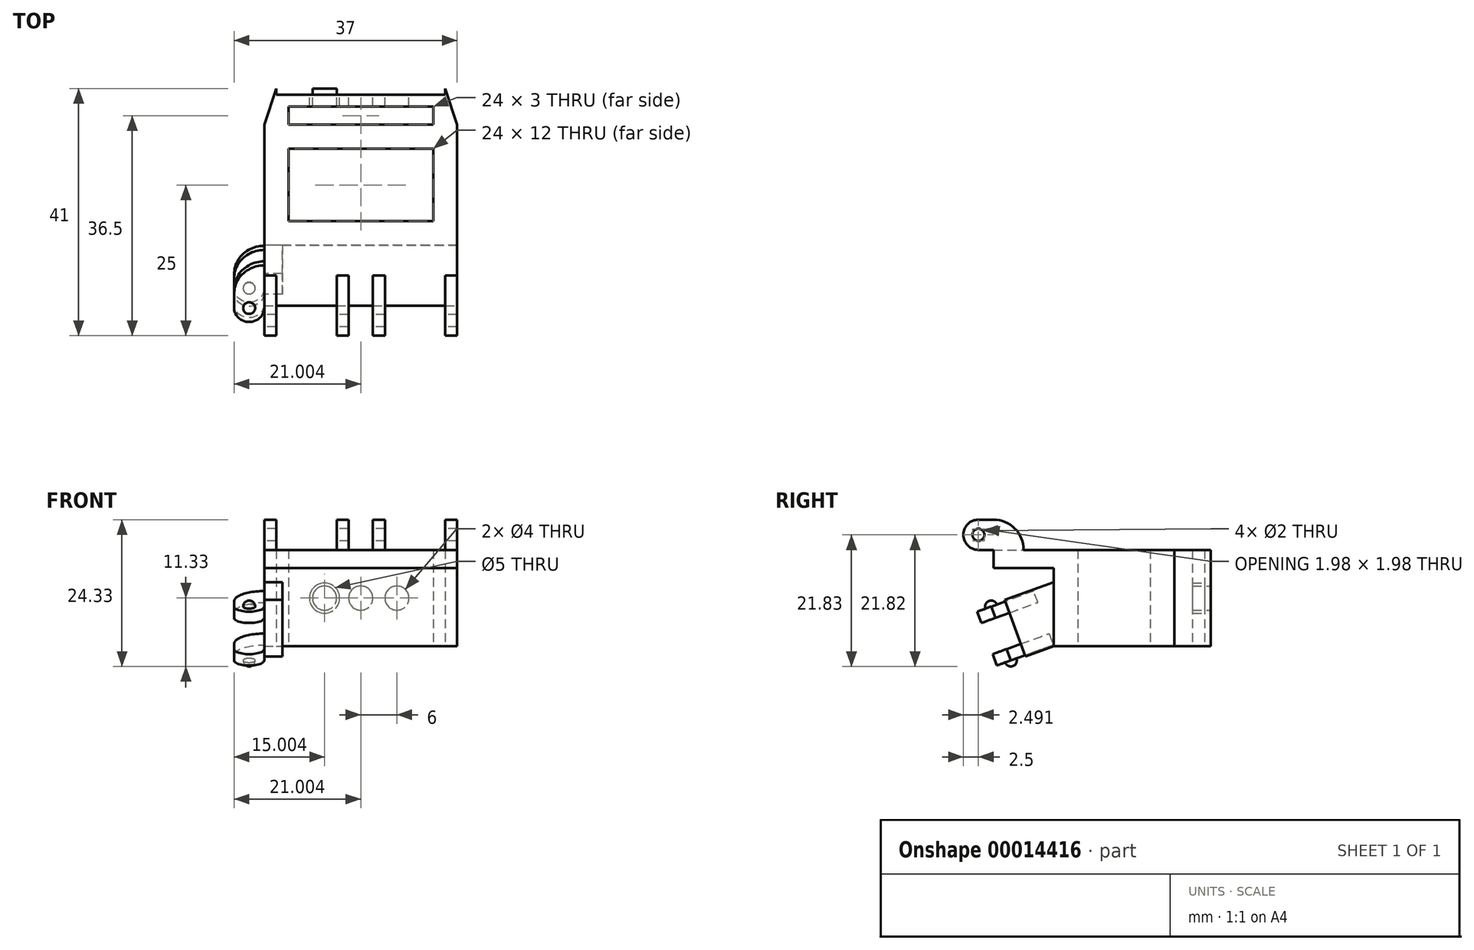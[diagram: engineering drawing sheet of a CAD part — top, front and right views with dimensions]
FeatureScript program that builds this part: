
annotation { "Feature Type Name" : "Feature", "Feature Type Description" : "" }
export const myFeature = defineFeature(function(context is Context, id is Id, definition is map)
    precondition{}
    {
        {
            var Q0;
            Q0=qCreatedBy(makeId("Top.planeOp"),FACE);
            var sketch = newSketch(context, id + "F0", { "sketchPlane" : qUnion([Q0])});
            skLineSegment(sketch, "E0.bottom", {"start": v(-11.62, 6.4) * mm, "end": v(12.38, 6.4) * mm});
            skLineSegment(sketch, "E0.top", {"start": v(-11.62, -5.6) * mm, "end": v(12.38, -5.6) * mm});
            skLineSegment(sketch, "E0.left", {"start": v(-11.62, 6.4) * mm, "end": v(-11.62, -5.6) * mm});
            skLineSegment(sketch, "E0.right", {"start": v(12.38, 6.4) * mm, "end": v(12.38, -5.6) * mm});
            skLineSegment(sketch, "E1.0", {"start": v(-15.62, 10.4) * mm, "end": v(16.38, 10.4) * mm});
            skLineSegment(sketch, "E1.1", {"start": v(-15.62, 10.4) * mm, "end": v(-15.62, -9.6) * mm});
            skLineSegment(sketch, "E1.2", {"start": v(-15.62, -9.6) * mm, "end": v(16.38, -9.6) * mm});
            skLineSegment(sketch, "E1.3", {"start": v(16.38, 10.4) * mm, "end": v(16.38, -9.6) * mm});
            skLineSegment(sketch, "E2", {"start": v(0.38, 10.4) * mm, "end": v(0.38, 16) * mm, "construction": true});
            skPoint(sketch, "E3", {"position": v(0.38, 13.4) * mm});
            skPoint(sketch, "E4", {"position": v(12.38, 10.4) * mm});
            skLineSegment(sketch, "E5", {"start": v(12.38, 10.4) * mm, "end": v(12.38, 13.4) * mm});
            skLineSegment(sketch, "E6", {"start": v(0.38, 13.4) * mm, "end": v(12.38, 13.4) * mm});
            skLineSegment(sketch, "E7.MirrorCS", {"start": v(0.38, 13.4) * mm, "end": v(-11.62, 13.4) * mm});
            skLineSegment(sketch, "E8.MirrorCS", {"start": v(-11.62, 10.4) * mm, "end": v(-11.62, 13.4) * mm});
            skPoint(sketch, "E9", {"position": v(0.38, 16.4) * mm});
            skLineSegment(sketch, "E10", {"start": v(0.38, 16.4) * mm, "end": v(14.38, 16.4) * mm});
            skLineSegment(sketch, "E11", {"start": v(16.38, 10.4) * mm, "end": v(14.38, 16.4) * mm});
            skLineSegment(sketch, "E12.MirrorCS", {"start": v(0.38, 16.4) * mm, "end": v(-13.62, 16.4) * mm});
            skLineSegment(sketch, "E13.MirrorCS", {"start": v(-15.62, 10.4) * mm, "end": v(-13.62, 16.4) * mm});
            skSolve(sketch);
        }
        {
            var Q0;
            Q0=makeQuery(id+"F0.imprint","IMPRINT",FACE,{"disambiguationData":[TD([[makeQuery(id+"F0.imprint","IMPRINT",EDGE,{"derivedFrom":sQuery(id+"F0.wireOp",EDGE,"E0.bottom")}),1.0]])]});
            var Q1;
            Q1=makeQuery(id+"F0.imprint","IMPRINT",FACE,{"disambiguationData":[TD([[makeQuery(id+"F0.imprint","IMPRINT",EDGE,{"derivedFrom":sQuery(id+"F0.wireOp",EDGE,"d9226599-e2ed-4d66-8e42-112def7345b0")}),1.0]])]});
            var Q2;
            {var subQ3=sQuery(id+"F0.wireOp",EDGE,"E5");Q2=makeQuery(id+"F0.imprint","IMPRINT",FACE,{"disambiguationData":[TD([[makeQuery(id+"F0.imprint","IMPRINT",EDGE,{"derivedFrom":subQ3}),-1.0]])]});}
            extrude(context, id + "F1", {"entities" : qUnion([Q0, Q1, Q2]), "depth" : 16 * mm});
        }
        {
            var Q0;
            Q0=makeQuery(id+"F1.opExtrude","SWEPT_FACE",FACE,{"disambiguationData":[OSD([sQuery(id+"F0.wireOp",EDGE,"E10"),sQuery(id+"F0.wireOp",EDGE,"E12.MirrorCS")])]});
            var sketch = newSketch(context, id + "F2", { "sketchPlane" : qUnion([Q0])});
            skLineSegment(sketch, "E14", {"start": v(-0.38, 16) * mm, "end": v(-0.38, 0) * mm, "construction": true});
            skLineSegment(sketch, "E15", {"start": v(-14.88, 8) * mm, "end": v(14.12, 8) * mm, "construction": true});
            skCircle(sketch, "E16", {"center": v(-0.38, 8) * mm, "radius": 2.5 * mm});
            skCircle(sketch, "E17", {"center": v(-0.38, 8) * mm, "radius": 2 * mm});
            skCircle(sketch, "E18", {"center": v(-6.38, 8) * mm, "radius": 2.5 * mm});
            skCircle(sketch, "E19", {"center": v(-6.38, 8) * mm, "radius": 2 * mm});
            skCircle(sketch, "E20.MirrorC", {"center": v(5.62, 8) * mm, "radius": 2.5 * mm});
            skCircle(sketch, "E21.MirrorC", {"center": v(5.62, 8) * mm, "radius": 2 * mm});
            skPoint(sketch, "E22", {"position": v(-14.38, 0) * mm});
            skPoint(sketch, "E23", {"position": v(13.62, 0) * mm});
            skLineSegment(sketch, "E24", {"start": v(-14.38, 16) * mm, "end": v(13.62, 0) * mm, "construction": true});
            skLineSegment(sketch, "E25", {"start": v(-14.38, 0) * mm, "end": v(13.62, 16) * mm, "construction": true});
            skSolve(sketch);
        }
        {
            var Q0;
            Q0=makeQuery(id+"F2.imprint","IMPRINT",FACE,{"disambiguationData":[TD([[makeQuery(id+"F2.imprint","IMPRINT",EDGE,{"derivedFrom":sQuery(id+"F2.wireOp",EDGE,"E19")}),1.0]])]});
            var Q1;
            Q1=makeQuery(id+"F2.imprint","IMPRINT",FACE,{"disambiguationData":[TD([[makeQuery(id+"F2.imprint","IMPRINT",EDGE,{"derivedFrom":sQuery(id+"F2.wireOp",EDGE,"E17")}),1.0]])]});
            var Q2;
            Q2=makeQuery(id+"F2.imprint","IMPRINT",FACE,{"disambiguationData":[TD([[makeQuery(id+"F2.imprint","IMPRINT",EDGE,{"derivedFrom":sQuery(id+"F2.wireOp",EDGE,"E21.MirrorC")}),-1.0]])]});
            extrude(context, id + "F3", {"entities" : qUnion([Q0, Q1, Q2]), "operationType" : NewBodyOperationType.REMOVE, "endBound" : BoundingType.UP_TO_NEXT, "oppositeDirection" : true, "depth" : 25 * mm});
        }
        {
            var Q0;
            Q0=makeQuery(id+"F2.imprint","IMPRINT",FACE,{"disambiguationData":[TD([[makeQuery(id+"F2.imprint","IMPRINT",EDGE,{"derivedFrom":sQuery(id+"F2.wireOp",EDGE,"E18")}),1.0]])]});
            var Q1;
            Q1=makeQuery(id+"F2.imprint","IMPRINT",FACE,{"disambiguationData":[TD([[makeQuery(id+"F2.imprint","IMPRINT",EDGE,{"derivedFrom":sQuery(id+"F2.wireOp",EDGE,"E20.MirrorC")}),-1.0]])]});
            var Q2;
            Q2=makeQuery(id+"F2.imprint","IMPRINT",FACE,{"disambiguationData":[TD([[makeQuery(id+"F2.imprint","IMPRINT",EDGE,{"derivedFrom":sQuery(id+"F2.wireOp",EDGE,"E16")}),1.0]])]});
            extrude(context, id + "F4", {"entities" : qUnion([Q0, Q1, Q2]), "operationType" : NewBodyOperationType.REMOVE, "oppositeDirection" : true, "depth" : 1 * mm});
        }
        {
            var Q0;
            Q0=makeQuery(id+"F1.opExtrude","SWEPT_FACE",FACE,{"disambiguationData":[OSD([sQuery(id+"F0.wireOp",EDGE,"E1.2")])]});
            var sketch = newSketch(context, id + "F5", { "sketchPlane" : qUnion([Q0])});
            skPoint(sketch, "E26", {"position": v(-15.62, 16) * mm});
            skPoint(sketch, "E27", {"position": v(-15.62, 13) * mm});
            skPoint(sketch, "E28", {"position": v(-12.62, 16) * mm});
            skLineSegment(sketch, "E29", {"start": v(-12.62, 16) * mm, "end": v(-12.62, 0) * mm, "construction": true});
            skLineSegment(sketch, "E30", {"start": v(-15.62, 13) * mm, "end": v(16.38, 13) * mm, "construction": true});
            skPoint(sketch, "E31", {"position": v(-12.62, 13) * mm});
            skLineSegment(sketch, "E32", {"start": v(16.38, 13) * mm, "end": v(-12.62, 13) * mm});
            skLineSegment(sketch, "E33", {"start": v(-12.62, 0) * mm, "end": v(-12.62, 13) * mm});
            skLineSegment(sketch, "E34", {"start": v(-15.62, 0) * mm, "end": v(-12.62, 0) * mm});
            skLineSegment(sketch, "E35", {"start": v(-15.62, 0) * mm, "end": v(-15.62, 16) * mm});
            skLineSegment(sketch, "E36", {"start": v(-15.62, 16) * mm, "end": v(16.38, 16) * mm});
            skLineSegment(sketch, "E37", {"start": v(16.38, 16) * mm, "end": v(16.38, 13) * mm});
            skSolve(sketch);
        }
        {
            var Q0;
            Q0=makeQuery(id+"F5.imprint","IMPRINT",FACE,{"disambiguationData":[TD([[makeQuery(id+"F5.imprint","IMPRINT",EDGE,{"derivedFrom":sQuery(id+"F5.wireOp",EDGE,"E32")}),-1.0]])]});
            extrude(context, id + "F6", {"entities" : qUnion([Q0]), "operationType" : NewBodyOperationType.ADD, "depth" : 10 * mm});
        }
        {
            var Q0;
            Q0=makeQuery(id+"F6.boolean.opBoolean","MERGE",FACE,{"derivedFrom":[makeQuery(id+"F1.opExtrude","CAP_FACE",FACE,{"disambiguationData":[OSD([sQuery(id+"F0.wireOp",EDGE,"E0.bottom"),sQuery(id+"F0.wireOp",EDGE,"E0.top"),sQuery(id+"F0.wireOp",EDGE,"E0.left"),sQuery(id+"F0.wireOp",EDGE,"E0.right"),sQuery(id+"F0.wireOp",EDGE,"E1.0"),sQuery(id+"F0.wireOp",EDGE,"E1.1"),sQuery(id+"F0.wireOp",EDGE,"E1.2"),sQuery(id+"F0.wireOp",EDGE,"E1.3"),sQuery(id+"F0.wireOp",EDGE,"E5"),sQuery(id+"F0.wireOp",EDGE,"E6"),sQuery(id+"F0.wireOp",EDGE,"E7.MirrorCS"),sQuery(id+"F0.wireOp",EDGE,"E8.MirrorCS"),sQuery(id+"F0.wireOp",EDGE,"E10"),sQuery(id+"F0.wireOp",EDGE,"E11"),sQuery(id+"F0.wireOp",EDGE,"E12.MirrorCS"),sQuery(id+"F0.wireOp",EDGE,"E13.MirrorCS")])],"isStart":false}),makeQuery(id+"F6.opExtrude","SWEPT_FACE",FACE,{"disambiguationData":[OSD([sQuery(id+"F5.wireOp",EDGE,"E36")])]})]});
            var sketch = newSketch(context, id + "F7", { "sketchPlane" : qUnion([Q0])});
            skPoint(sketch, "E38", {"position": v(-15.62, -19.6) * mm});
            skPoint(sketch, "E39", {"position": v(-13.62, -19.6) * mm});
            skPoint(sketch, "E40", {"position": v(0.38, -19.6) * mm});
            skLineSegment(sketch, "E41", {"start": v(-15.62, -19.6) * mm, "end": v(-15.62, -24.6) * mm, "construction": true});
            skLineSegment(sketch, "E42", {"start": v(-13.62, -19.6) * mm, "end": v(-13.62, -24.6) * mm, "construction": true});
            skLineSegment(sketch, "E43", {"start": v(-15.62, -19.6) * mm, "end": v(-15.62, -14.6) * mm, "construction": true});
            skLineSegment(sketch, "E44", {"start": v(-13.62, -19.6) * mm, "end": v(-13.62, -14.6) * mm, "construction": true});
            skLineSegment(sketch, "E45", {"start": v(-15.62, -14.6) * mm, "end": v(-13.62, -14.6) * mm});
            skLineSegment(sketch, "E46", {"start": v(-13.62, -24.6) * mm, "end": v(-13.62, -14.6) * mm});
            skLineSegment(sketch, "E47", {"start": v(-15.62, -24.6) * mm, "end": v(-15.62, -14.6) * mm});
            skLineSegment(sketch, "E48", {"start": v(-15.62, -24.6) * mm, "end": v(-13.62, -24.6) * mm});
            skLineSegment(sketch, "E49", {"start": v(0.38, -19.6) * mm, "end": v(0.38, -13.68) * mm, "construction": true});
            skLineSegment(sketch, "E50.MirrorCS", {"start": v(14.38, -24.6) * mm, "end": v(14.38, -14.6) * mm});
            skLineSegment(sketch, "E51.MirrorCS", {"start": v(16.38, -24.6) * mm, "end": v(16.38, -14.6) * mm});
            skLineSegment(sketch, "E52.MirrorCS", {"start": v(16.38, -14.6) * mm, "end": v(14.38, -14.6) * mm});
            skLineSegment(sketch, "E53.MirrorCS", {"start": v(16.38, -24.6) * mm, "end": v(14.38, -24.6) * mm});
            skPoint(sketch, "E54", {"position": v(-8.62, -19.6) * mm});
            skLineSegment(sketch, "E55", {"start": v(-8.62, -19.6) * mm, "end": v(-8.62, -14.6) * mm, "construction": true});
            skLineSegment(sketch, "E56.MirrorCS", {"start": v(-1.62, -24.6) * mm, "end": v(-1.62, -14.6) * mm});
            skLineSegment(sketch, "E57.MirrorCS", {"start": v(-3.62, -24.6) * mm, "end": v(-3.62, -14.6) * mm});
            skLineSegment(sketch, "E58.MirrorCS", {"start": v(-1.62, -24.6) * mm, "end": v(-3.62, -24.6) * mm});
            skLineSegment(sketch, "E59.MirrorCS", {"start": v(-1.62, -14.6) * mm, "end": v(-3.62, -14.6) * mm});
            skLineSegment(sketch, "E60.MirrorCS", {"start": v(2.38, -24.6) * mm, "end": v(2.38, -14.6) * mm});
            skLineSegment(sketch, "E61.MirrorCS", {"start": v(4.38, -24.6) * mm, "end": v(4.38, -14.6) * mm});
            skLineSegment(sketch, "E62.MirrorCS", {"start": v(2.38, -14.6) * mm, "end": v(4.38, -14.6) * mm});
            skLineSegment(sketch, "E63.MirrorCS", {"start": v(2.38, -24.6) * mm, "end": v(4.38, -24.6) * mm});
            skSolve(sketch);
        }
        {
            var Q0;
            {var subQ5=sQuery(id+"F7.wireOp",EDGE,"E45");Q0=makeQuery(id+"F7.imprint","IMPRINT",FACE,{"disambiguationData":[TD([[makeQuery(id+"F7.imprint","IMPRINT",EDGE,{"derivedFrom":subQ5}),-1.0]])]});}
            var Q1;
            {var subQ5=sQuery(id+"F7.wireOp",EDGE,"E48");Q1=makeQuery(id+"F7.imprint","IMPRINT",FACE,{"disambiguationData":[TD([[makeQuery(id+"F7.imprint","IMPRINT",EDGE,{"derivedFrom":subQ5}),1.0]])]});}
            var Q2;
            {var subQ5=sQuery(id+"F7.wireOp",EDGE,"E53.MirrorCS");Q2=makeQuery(id+"F7.imprint","IMPRINT",FACE,{"disambiguationData":[TD([[makeQuery(id+"F7.imprint","IMPRINT",EDGE,{"derivedFrom":subQ5}),-1.0]])]});}
            var Q3;
            {var subQ0=sQuery(id+"F7.wireOp",EDGE,"E52.MirrorCS");Q3=makeQuery(id+"F7.imprint","IMPRINT",FACE,{"disambiguationData":[TD([[makeQuery(id+"F7.imprint","IMPRINT",EDGE,{"derivedFrom":subQ0}),1.0]])]});}
            var Q4;
            {var subQ5=sQuery(id+"F7.wireOp",EDGE,"E59.MirrorCS");Q4=makeQuery(id+"F7.imprint","IMPRINT",FACE,{"disambiguationData":[TD([[makeQuery(id+"F7.imprint","IMPRINT",EDGE,{"derivedFrom":subQ5}),1.0]])]});}
            var Q5;
            {var subQ5=sQuery(id+"F7.wireOp",EDGE,"E58.MirrorCS");Q5=makeQuery(id+"F7.imprint","IMPRINT",FACE,{"disambiguationData":[TD([[makeQuery(id+"F7.imprint","IMPRINT",EDGE,{"derivedFrom":subQ5}),-1.0]])]});}
            var Q6;
            {var subQ0=sQuery(id+"F7.wireOp",EDGE,"E62.MirrorCS");Q6=makeQuery(id+"F7.imprint","IMPRINT",FACE,{"disambiguationData":[TD([[makeQuery(id+"F7.imprint","IMPRINT",EDGE,{"derivedFrom":subQ0}),-1.0]])]});}
            var Q7;
            {var subQ5=sQuery(id+"F7.wireOp",EDGE,"E63.MirrorCS");Q7=makeQuery(id+"F7.imprint","IMPRINT",FACE,{"disambiguationData":[TD([[makeQuery(id+"F7.imprint","IMPRINT",EDGE,{"derivedFrom":subQ5}),1.0]])]});}
            extrude(context, id + "F8", {"entities" : qUnion([Q0, Q1, Q2, Q3, Q4, Q5, Q6, Q7]), "operationType" : NewBodyOperationType.ADD, "depth" : 5 * mm});
        }
        {
            var Q0;
            Q0=makeQuery(id+"F6.opExtrude","CAP_FACE",FACE,{"disambiguationData":[OSD([sQuery(id+"F5.wireOp",EDGE,"E32"),sQuery(id+"F5.wireOp",EDGE,"E33"),sQuery(id+"F5.wireOp",EDGE,"E34"),sQuery(id+"F5.wireOp",EDGE,"E35"),sQuery(id+"F5.wireOp",EDGE,"E36"),sQuery(id+"F5.wireOp",EDGE,"E37")])],"isStart":false});
            var sketch = newSketch(context, id + "F9", { "sketchPlane" : qUnion([Q0])});
            skPoint(sketch, "E64", {"position": v(-12.62, 13) * mm});
            skLineSegment(sketch, "E65", {"start": v(-12.62, 13) * mm, "end": v(-15.62, 13) * mm});
            skSolve(sketch);
        }
        {
            var Q0;
            {var subQ1=sQuery(id+"F9.wireOp",EDGE,"E65");Q0=makeQuery(id+"F9.imprint","IMPRINT",FACE,{"disambiguationData":[TD([[makeQuery(id+"F9.imprint","IMPRINT",EDGE,{"derivedFrom":subQ1}),1.0]])]});}
            extrude(context, id + "F10", {"entities" : qUnion([Q0]), "operationType" : NewBodyOperationType.REMOVE, "oppositeDirection" : true, "depth" : 10 * mm});
        }
        {
            var Q0;
            Q0=makeQuery(id+"F6.boolean.opBoolean","MERGE",FACE,{"derivedFrom":[makeQuery(id+"F1.opExtrude","SWEPT_FACE",FACE,{"disambiguationData":[OSD([sQuery(id+"F0.wireOp",EDGE,"E1.1")])]}),makeQuery(id+"F6.opExtrude","SWEPT_FACE",FACE,{"disambiguationData":[OSD([sQuery(id+"F5.wireOp",EDGE,"E35")])]})]});
            var sketch = newSketch(context, id + "F11", { "sketchPlane" : qUnion([Q0])});
            skPoint(sketch, "E66", {"position": v(9.6, 0) * mm});
            skPoint(sketch, "E67", {"position": v(9.6, 13) * mm});
            skPoint(sketch, "E68", {"position": v(9.6, 6.5) * mm});
            skLineSegment(sketch, "E69", {"start": v(9.6, 0) * mm, "end": v(14.3, -1.71) * mm, "construction": true});
            skLineSegment(sketch, "E70", {"start": v(9.6, 0) * mm, "end": v(9.6, 6.5) * mm, "construction": true});
            skLineSegment(sketch, "E71", {"start": v(14.3, -1.71) * mm, "end": v(17.72, 7.69) * mm, "construction": true});
            skLineSegment(sketch, "E72", {"start": v(17.72, 7.69) * mm, "end": v(9.6, 10.64) * mm, "construction": true});
            skLineSegment(sketch, "E73", {"start": v(9.6, 10.64) * mm, "end": v(17.72, 7.69) * mm});
            skLineSegment(sketch, "E74", {"start": v(17.72, 7.69) * mm, "end": v(14.3, -1.71) * mm});
            skLineSegment(sketch, "E75", {"start": v(14.3, -1.71) * mm, "end": v(9.6, 0) * mm});
            skLineSegment(sketch, "E76", {"start": v(9.6, 0) * mm, "end": v(9.6, 10.64) * mm});
            skSolve(sketch);
        }
        {
            var Q0;
            Q0=makeQuery(id+"F11.imprint","IMPRINT",FACE,{"disambiguationData":[TD([[makeQuery(id+"F11.imprint","IMPRINT",EDGE,{"derivedFrom":sQuery(id+"F11.wireOp",EDGE,"E73")}),-1.0]])]});
            extrude(context, id + "F12", {"entities" : qUnion([Q0]), "operationType" : NewBodyOperationType.ADD, "oppositeDirection" : true, "depth" : 3 * mm});
        }
        {
            var Q0;
            Q0=makeQuery(id+"F12.boolean.opBoolean","MERGE",FACE,{"derivedFrom":[makeQuery(id+"F6.boolean.opBoolean","MERGE",FACE,{"derivedFrom":[makeQuery(id+"F1.opExtrude","SWEPT_FACE",FACE,{"disambiguationData":[OSD([sQuery(id+"F0.wireOp",EDGE,"E1.1")])]}),makeQuery(id+"F6.opExtrude","SWEPT_FACE",FACE,{"disambiguationData":[OSD([sQuery(id+"F5.wireOp",EDGE,"E35")])]})]}),makeQuery(id+"F12.opExtrude","CAP_FACE",FACE,{"disambiguationData":[OSD([sQuery(id+"F11.wireOp",EDGE,"E73"),sQuery(id+"F11.wireOp",EDGE,"E74"),sQuery(id+"F11.wireOp",EDGE,"E75"),sQuery(id+"F11.wireOp",EDGE,"E76")])],"isStart":true})]});
            var sketch = newSketch(context, id + "F13", { "sketchPlane" : qUnion([Q0])});
            skPoint(sketch, "E77", {"position": v(17.72, 7.69) * mm});
            skPoint(sketch, "E78", {"position": v(16, 2.99) * mm});
            skPoint(sketch, "E79", {"position": v(16.95, 5.57) * mm});
            skLineSegment(sketch, "E80", {"start": v(16, 2.99) * mm, "end": v(13.28, 3.98) * mm, "construction": true});
            skLineSegment(sketch, "E81", {"start": v(17.72, 7.69) * mm, "end": v(22.42, 5.98) * mm, "construction": true});
            skLineSegment(sketch, "E82", {"start": v(16.95, 5.57) * mm, "end": v(21.65, 3.86) * mm, "construction": true});
            skLineSegment(sketch, "E83", {"start": v(21.65, 3.86) * mm, "end": v(16.95, 5.57) * mm});
            skPoint(sketch, "E84", {"position": v(13.02, 9.4) * mm});
            skLineSegment(sketch, "E85", {"start": v(21.65, 3.86) * mm, "end": v(12.25, 7.28) * mm});
            skLineSegment(sketch, "E86.MirrorCS", {"start": v(19.77, -1.3) * mm, "end": v(10.37, 2.11) * mm});
            skLineSegment(sketch, "E87", {"start": v(12.25, 7.28) * mm, "end": v(12.93, 9.16) * mm});
            skLineSegment(sketch, "E88.MirrorCS", {"start": v(21.65, 3.86) * mm, "end": v(22.33, 5.74) * mm});
            skLineSegment(sketch, "E89", {"start": v(12.93, 9.16) * mm, "end": v(22.33, 5.74) * mm});
            skLineSegment(sketch, "E90.MirrorCS", {"start": v(10.37, 2.11) * mm, "end": v(9.69, 0.23) * mm});
            skLineSegment(sketch, "E91.MirrorCS", {"start": v(9.69, 0.23) * mm, "end": v(19.08, -3.19) * mm});
            skLineSegment(sketch, "E92.MirrorCS", {"start": v(19.77, -1.3) * mm, "end": v(19.08, -3.19) * mm});
            skSolve(sketch);
        }
        {
            var Q0;
            {var subQ1=sQuery(id+"F13.wireOp",EDGE,"27cdea62-a975-46e6-88ea-ef7a49258366");Q0=makeQuery(id+"F13.imprint","IMPRINT",FACE,{"disambiguationData":[TD([[makeQuery(id+"F13.imprint","IMPRINT",EDGE,{"derivedFrom":subQ1}),-1.0]])]});}
            var Q1;
            {var subQ3=sQuery(id+"F13.wireOp",EDGE,"4966c16b-bf24-40fc-986f-31c6d37c2082");Q1=makeQuery(id+"F13.imprint","IMPRINT",FACE,{"disambiguationData":[TD([[makeQuery(id+"F13.imprint","IMPRINT",EDGE,{"derivedFrom":subQ3}),-1.0]])]});}
            var Q2;
            {var subQ4=sQuery(id+"F13.wireOp",EDGE,"a727023f-dfa3-4c32-8afa-23e3bec39dac0.MirrorCS");Q2=makeQuery(id+"F13.imprint","IMPRINT",FACE,{"disambiguationData":[TD([[makeQuery(id+"F13.imprint","IMPRINT",EDGE,{"derivedFrom":subQ4}),1.0]])]});}
            var Q3;
            {var subQ3=sQuery(id+"F13.wireOp",EDGE,"6426e7fb-16d1-409e-b700-4e2e672a5eb60.MirrorCS");Q3=makeQuery(id+"F13.imprint","IMPRINT",FACE,{"disambiguationData":[TD([[makeQuery(id+"F13.imprint","IMPRINT",EDGE,{"derivedFrom":subQ3}),1.0]])]});}
            var Q4;
            {var subQ5=sQuery(id+"F13.wireOp",EDGE,"E87");Q4=makeQuery(id+"F13.imprint","IMPRINT",FACE,{"disambiguationData":[TD([[makeQuery(id+"F13.imprint","IMPRINT",EDGE,{"derivedFrom":subQ5}),-1.0]])]});}
            var Q5;
            {var subQ5=sQuery(id+"F13.wireOp",EDGE,"E88.MirrorCS");Q5=makeQuery(id+"F13.imprint","IMPRINT",FACE,{"disambiguationData":[TD([[makeQuery(id+"F13.imprint","IMPRINT",EDGE,{"derivedFrom":subQ5}),1.0]])]});}
            var Q6;
            {var subQ5=sQuery(id+"F13.wireOp",EDGE,"E90.MirrorCS");Q6=makeQuery(id+"F13.imprint","IMPRINT",FACE,{"disambiguationData":[TD([[makeQuery(id+"F13.imprint","IMPRINT",EDGE,{"derivedFrom":subQ5}),1.0]])]});}
            var Q7;
            {var subQ5=sQuery(id+"F13.wireOp",EDGE,"E92.MirrorCS");Q7=makeQuery(id+"F13.imprint","IMPRINT",FACE,{"disambiguationData":[TD([[makeQuery(id+"F13.imprint","IMPRINT",EDGE,{"derivedFrom":subQ5}),-1.0]])]});}
            extrude(context, id + "F14", {"entities" : qUnion([Q0, Q1, Q2, Q3, Q4, Q5, Q6, Q7]), "operationType" : NewBodyOperationType.ADD, "depth" : 5 * mm});
        }
        {
            var Q0;
            Q0=makeQuery(id+"F14.opExtrude","SWEPT_FACE",FACE,{"disambiguationData":[OSD([sQuery(id+"F13.wireOp",EDGE,"E91.MirrorCS")])]});
            var sketch = newSketch(context, id + "F15", { "sketchPlane" : qUnion([Q0])});
            skPoint(sketch, "E93", {"position": v(-15.62, 14.02) * mm});
            skPoint(sketch, "E94", {"position": v(-15.62, 19.02) * mm});
            skPoint(sketch, "E95", {"position": v(-20.62, 19.02) * mm});
            skPoint(sketch, "E96", {"position": v(-20.62, 14.02) * mm});
            skLineSegment(sketch, "E97", {"start": v(-20.62, 19.02) * mm, "end": v(-15.62, 14.02) * mm, "construction": true});
            skLineSegment(sketch, "E98", {"start": v(-20.62, 14.02) * mm, "end": v(-15.62, 19.02) * mm, "construction": true});
            skLineSegment(sketch, "E99", {"start": v(-15.62, 16.52) * mm, "end": v(-20.62, 16.52) * mm, "construction": true});
            skCircle(sketch, "E100", {"center": v(-18.12, 16.52) * mm, "radius": 1 * mm});
            skPoint(sketch, "E101", {"position": v(-15.62, 9.02) * mm});
            skArc(sketch, "E102", {"start": v(-20.62, 14.02) * mm, "mid": v(-19.15, 10.49) * mm, "end": v(-15.62, 9.02) * mm});
            skArc(sketch, "E103", {"start": v(-15.62, 16.52) * mm, "mid": v(-18.12, 19) * mm, "end": v(-20.62, 16.52) * mm});
            skSolve(sketch);
        }
        {
            var Q0;
            Q0=makeQuery(id+"F14.opExtrude","SWEPT_FACE",FACE,{"disambiguationData":[OSD([sQuery(id+"F13.wireOp",EDGE,"E89")])]});
            var sketch = newSketch(context, id + "F16", { "sketchPlane" : qUnion([Q0])});
            skPoint(sketch, "E104", {"position": v(-15.62, -19.02) * mm});
            skPoint(sketch, "E105", {"position": v(-15.62, -14.02) * mm});
            skPoint(sketch, "E106", {"position": v(-20.62, -19.02) * mm});
            skPoint(sketch, "E107", {"position": v(-20.62, -14.02) * mm});
            skLineSegment(sketch, "E108", {"start": v(-20.62, -14.02) * mm, "end": v(-15.62, -19.02) * mm, "construction": true});
            skLineSegment(sketch, "E109", {"start": v(-20.62, -19.02) * mm, "end": v(-15.62, -14.02) * mm, "construction": true});
            skCircle(sketch, "E110", {"center": v(-18.12, -16.52) * mm, "radius": 1 * mm});
            skSolve(sketch);
        }
        {
            var Q0;
            Q0=makeQuery(id+"F16.imprint","IMPRINT",FACE,{"disambiguationData":[TD([[makeQuery(id+"F16.imprint","IMPRINT",EDGE,{"derivedFrom":sQuery(id+"F16.wireOp",EDGE,"E110")}),1.0]])]});
            extrude(context, id + "F17", {"entities" : qUnion([Q0]), "operationType" : NewBodyOperationType.ADD, "depth" : 1 * mm});
        }
        {
            var Q0;
            Q0=makeQuery(id+"F15.imprint","IMPRINT",FACE,{"disambiguationData":[TD([[makeQuery(id+"F15.imprint","IMPRINT",EDGE,{"derivedFrom":sQuery(id+"F15.wireOp",EDGE,"E100")}),1.0]])]});
            extrude(context, id + "F18", {"entities" : qUnion([Q0]), "operationType" : NewBodyOperationType.ADD, "depth" : 1 * mm});
        }
        {
            var Q0;
            {var subQ3=sQuery(id+"F15.wireOp",EDGE,"E103");Q0=makeQuery(id+"F15.imprint","IMPRINT",FACE,{"disambiguationData":[TD([[makeQuery(id+"F15.imprint","IMPRINT",EDGE,{"derivedFrom":subQ3}),-1.0]])]});}
            var Q1;
            {var subQ2=sQuery(id+"F15.wireOp",EDGE,"E102");Q1=makeQuery(id+"F15.imprint","IMPRINT",FACE,{"disambiguationData":[TD([[makeQuery(id+"F15.imprint","IMPRINT",EDGE,{"derivedFrom":subQ2}),-1.0]])]});}
            extrude(context, id + "F19", {"entities" : qUnion([Q0, Q1]), "operationType" : NewBodyOperationType.REMOVE, "endBound" : BoundingType.THROUGH_ALL, "oppositeDirection" : true, "depth" : 25 * mm});
        }
        {
            var Q0;
            Q0=makeQuery(id+"F12.boolean.opBoolean","MERGE",FACE,{"derivedFrom":[makeQuery(id+"F8.boolean.opBoolean","MERGE",FACE,{"derivedFrom":[makeQuery(id+"F6.boolean.opBoolean","MERGE",FACE,{"derivedFrom":[makeQuery(id+"F1.opExtrude","SWEPT_FACE",FACE,{"disambiguationData":[OSD([sQuery(id+"F0.wireOp",EDGE,"E1.1")])]}),makeQuery(id+"F6.opExtrude","SWEPT_FACE",FACE,{"disambiguationData":[OSD([sQuery(id+"F5.wireOp",EDGE,"E35")])]})]}),makeQuery(id+"F8.opExtrude","SWEPT_FACE",FACE,{"disambiguationData":[OSD([sQuery(id+"F7.wireOp",EDGE,"E47")])]})]}),makeQuery(id+"F12.opExtrude","CAP_FACE",FACE,{"disambiguationData":[OSD([sQuery(id+"F11.wireOp",EDGE,"E73"),sQuery(id+"F11.wireOp",EDGE,"E74"),sQuery(id+"F11.wireOp",EDGE,"E75"),sQuery(id+"F11.wireOp",EDGE,"E76")])],"isStart":true})]});
            var sketch = newSketch(context, id + "F20", { "sketchPlane" : qUnion([Q0])});
            skPoint(sketch, "E111", {"position": v(19.6, 16) * mm});
            skPoint(sketch, "E112", {"position": v(24.6, 21) * mm});
            skPoint(sketch, "E113", {"position": v(24.6, 16) * mm});
            skLineSegment(sketch, "E114", {"start": v(19.6, 16) * mm, "end": v(19.6, 21) * mm, "construction": true});
            skLineSegment(sketch, "E115", {"start": v(19.6, 21) * mm, "end": v(24.6, 16) * mm, "construction": true});
            skLineSegment(sketch, "E116", {"start": v(19.6, 16) * mm, "end": v(24.6, 21) * mm, "construction": true});
            skPoint(sketch, "E117", {"position": v(22.1, 18.5) * mm});
            skCircle(sketch, "E118", {"center": v(22.1, 18.5) * mm, "radius": 1 * mm});
            skPoint(sketch, "E119", {"position": v(14.6, 16) * mm});
            skArc(sketch, "E120", {"start": v(19.6, 21) * mm, "mid": v(16.06, 19.54) * mm, "end": v(14.6, 16) * mm});
            skPoint(sketch, "E121", {"position": v(22.1, 21) * mm});
            skPoint(sketch, "E122", {"position": v(22.1, 16) * mm});
            skArc(sketch, "E123", {"start": v(22.1, 16) * mm, "mid": v(24.6, 18.5) * mm, "end": v(22.1, 21) * mm});
            skLineSegment(sketch, "E124", {"start": v(19.6, 16) * mm, "end": v(19.6, 21) * mm});
            skLineSegment(sketch, "E125", {"start": v(22.1, 21) * mm, "end": v(19.6, 21) * mm});
            skLineSegment(sketch, "E126", {"start": v(19.6, 16) * mm, "end": v(22.1, 16) * mm});
            skSolve(sketch);
        }
        {
            var Q0;
            {var subQ2=sQuery(id+"F20.wireOp",EDGE,"E120");Q0=makeQuery(id+"F20.imprint","IMPRINT",FACE,{"disambiguationData":[TD([[makeQuery(id+"F20.imprint","IMPRINT",EDGE,{"derivedFrom":subQ2}),-1.0]])]});}
            var Q1;
            {var subQ0=sQuery(id+"F20.wireOp",EDGE,"E123");var subQ1=sQuery(id+"F7.wireOp",EDGE,"E47");var subQ2=makeQuery(id+"F8.opExtrude","CAP_EDGE",EDGE,{"disambiguationData":[OSD([subQ1])],"isStart":false});var subQ3=makeQuery(id+"F20.imprint","INTERSECT",VERTEX,{"derivedFrom":[subQ2,subQ0,sQuery(id+"F20.wireOp",EDGE,"E125")]});Q1=makeQuery(id+"F20.imprint","IMPRINT",FACE,{"disambiguationData":[TD([[makeQuery(id+"F20.imprint","IMPRINT",EDGE,{"disambiguationData":[TD([[subQ3,1.0]])],"derivedFrom":subQ0}),-1.0]])]});}
            var Q2;
            {var subQ0=sQuery(id+"F20.wireOp",EDGE,"E123");var subQ1=sQuery(id+"F7.wireOp",EDGE,"E47");var subQ2=makeQuery(id+"F8.opExtrude","CAP_EDGE",EDGE,{"disambiguationData":[OSD([subQ1])],"isStart":true});var subQ3=makeQuery(id+"F20.imprint","INTERSECT",VERTEX,{"derivedFrom":[subQ2,subQ0,sQuery(id+"F20.wireOp",EDGE,"E126")]});Q2=makeQuery(id+"F20.imprint","IMPRINT",FACE,{"disambiguationData":[TD([[makeQuery(id+"F20.imprint","IMPRINT",EDGE,{"disambiguationData":[TD([[subQ3,-1.0]])],"derivedFrom":subQ0}),-1.0]])]});}
            var Q3;
            Q3=makeQuery(id+"F20.imprint","IMPRINT",FACE,{"disambiguationData":[TD([[makeQuery(id+"F20.imprint","IMPRINT",EDGE,{"derivedFrom":sQuery(id+"F20.wireOp",EDGE,"E118")}),1.0]])]});
            extrude(context, id + "F21", {"entities" : qUnion([Q0, Q1, Q2, Q3]), "operationType" : NewBodyOperationType.REMOVE, "endBound" : BoundingType.THROUGH_ALL, "oppositeDirection" : true, "depth" : 25 * mm});
        }
        {
            var Q0;
            Q0=makeQuery(id+"F8.opExtrude","CAP_FACE",FACE,{"disambiguationData":[OSD([sQuery(id+"F7.wireOp",EDGE,"E45"),sQuery(id+"F7.wireOp",EDGE,"E46"),sQuery(id+"F7.wireOp",EDGE,"E48"),sQuery(id+"F7.wireOp",EDGE,"E47")])],"isStart":false});
            var sketch = newSketch(context, id + "F22", { "sketchPlane" : qUnion([Q0])});
            skPoint(sketch, "E127", {"position": v(-14.62, -19.6) * mm});
            skLineSegment(sketch, "E128", {"start": v(-14.62, -20.6) * mm, "end": v(-14.62, -24.6) * mm});
            skLineSegment(sketch, "E129", {"start": v(-14.62, -24.6) * mm, "end": v(-8.62, -24.6) * mm});
            skLineSegment(sketch, "E130", {"start": v(-8.62, -24.6) * mm, "end": v(-8.62, -20.6) * mm});
            skLineSegment(sketch, "E131", {"start": v(-13.62, -19.6) * mm, "end": v(-9.62, -19.6) * mm});
            skArc(sketch, "E132.filletArc", {"start": v(-13.62, -19.6) * mm, "mid": v(-14.32, -19.9) * mm, "end": v(-14.62, -20.6) * mm});
            skPoint(sketch, "E133.visualSharp", {"position": v(-8.62, -19.6) * mm});
            skArc(sketch, "E133.filletArc", {"start": v(-8.62, -20.6) * mm, "mid": v(-8.9, -19.9) * mm, "end": v(-9.62, -19.6) * mm});
            skSolve(sketch);
        }
        {
            var Q0;
            Q0=makeQuery(id+"F8.opExtrude","CAP_FACE",FACE,{"disambiguationData":[OSD([sQuery(id+"F7.wireOp",EDGE,"E60.MirrorCS"),sQuery(id+"F7.wireOp",EDGE,"E61.MirrorCS"),sQuery(id+"F7.wireOp",EDGE,"E62.MirrorCS"),sQuery(id+"F7.wireOp",EDGE,"E63.MirrorCS")])],"isStart":false});
            var sketch = newSketch(context, id + "F23", { "sketchPlane" : qUnion([Q0])});
            skPoint(sketch, "E134", {"position": v(3.38, -19.6) * mm});
            skLineSegment(sketch, "E135", {"start": v(3.38, -20.6) * mm, "end": v(3.38, -24.6) * mm});
            skLineSegment(sketch, "E136", {"start": v(3.38, -24.6) * mm, "end": v(9.38, -24.6) * mm});
            skLineSegment(sketch, "E137", {"start": v(9.38, -24.6) * mm, "end": v(9.38, -20.6) * mm});
            skLineSegment(sketch, "E138", {"start": v(4.38, -19.6) * mm, "end": v(8.38, -19.6) * mm});
            skArc(sketch, "E139.filletArc", {"start": v(4.38, -19.6) * mm, "mid": v(3.68, -19.9) * mm, "end": v(3.38, -20.6) * mm});
            skPoint(sketch, "E140.visualSharp", {"position": v(9.38, -19.6) * mm});
            skArc(sketch, "E140.filletArc", {"start": v(9.38, -20.6) * mm, "mid": v(9.1, -19.9) * mm, "end": v(8.38, -19.6) * mm});
            skSolve(sketch);
        }
        {
            var Q0;
            Q0=makeQuery(id+"F17.opExtrude","CAP_EDGE",EDGE,{"disambiguationData":[OSD([sQuery(id+"F16.wireOp",EDGE,"E110")])],"isStart":false});
            var Q1;
            Q1=makeQuery(id+"F18.opExtrude","CAP_EDGE",EDGE,{"disambiguationData":[OSD([sQuery(id+"F15.wireOp",EDGE,"E100")])],"isStart":false});
            fillet(context, id + "F24", {"entities" : qUnion([Q0, Q1]), "radius" : 1 * mm, "tangentPropagation" : true, "allowEdgeOverflow" : false});
        }
    });
